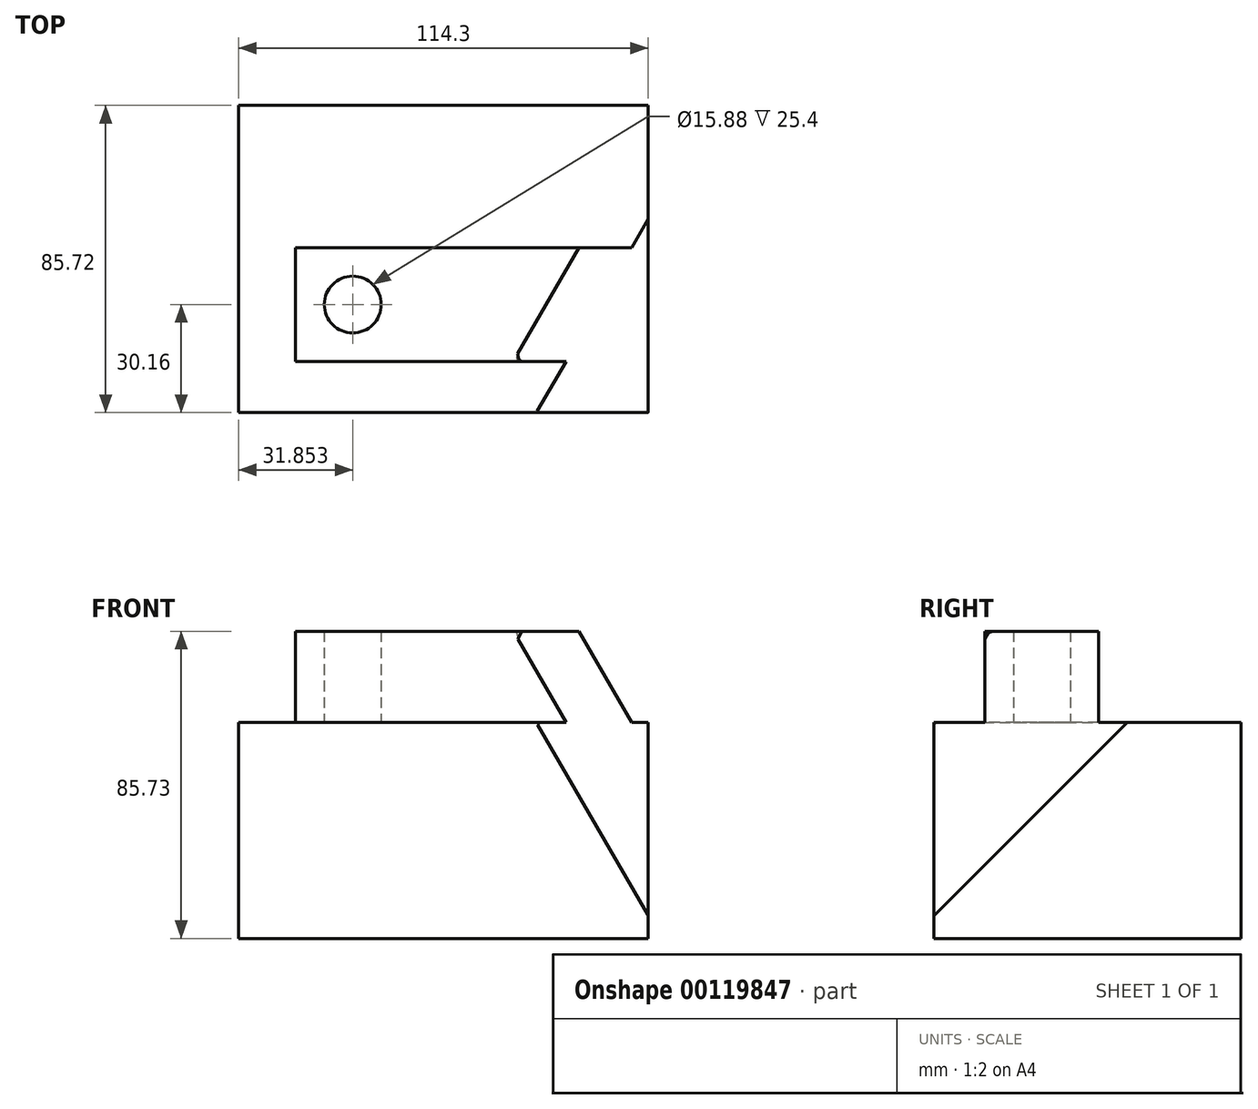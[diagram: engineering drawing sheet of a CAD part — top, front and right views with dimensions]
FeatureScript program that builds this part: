
annotation { "Feature Type Name" : "Feature", "Feature Type Description" : "" }
export const myFeature = defineFeature(function(context is Context, id is Id, definition is map)
    precondition{}
    {
        {
            var Q0;
            Q0=qCreatedBy(makeId("Front.planeOp"),FACE);
            var sketch = newSketch(context, id + "F0", { "sketchPlane" : qUnion([Q0])});
            skLineSegment(sketch, "E0", {"start": v(0, 0) * mm, "end": v(114.3, 0) * mm});
            skLineSegment(sketch, "E1", {"start": v(114.3, 0) * mm, "end": v(114.3, 60.33) * mm});
            skLineSegment(sketch, "E2", {"start": v(114.3, 60.33) * mm, "end": v(0, 60.33) * mm});
            skLineSegment(sketch, "E3", {"start": v(0, 60.33) * mm, "end": v(0, 0) * mm});
            skSolve(sketch);
        }
        {
            var Q0;
            Q0 = qSketchRegion(id + "F0", true);
            extrude(context, id + "F1", {"entities" : qUnion([Q0]), "endBound" : BoundingType.SYMMETRIC, "depth" : 85.72 * mm});
        }
        {
            var Q0;
            Q0=makeQuery(id+"F1.opExtrude","SWEPT_FACE",FACE,{"disambiguationData":[OSD([sQuery(id+"F0.wireOp",EDGE,"E2")])]});
            var sketch = newSketch(context, id + "F2", { "sketchPlane" : qUnion([Q0])});
            skLineSegment(sketch, "E4.bottom", {"start": v(15.88, 3.18) * mm, "end": v(114.3, 3.18) * mm});
            skLineSegment(sketch, "E4.top", {"start": v(15.88, -28.57) * mm, "end": v(114.3, -28.57) * mm});
            skLineSegment(sketch, "E4.left", {"start": v(15.88, 3.18) * mm, "end": v(15.88, -28.57) * mm});
            skLineSegment(sketch, "E4.right", {"start": v(114.3, 3.18) * mm, "end": v(114.3, -28.57) * mm});
            skSolve(sketch);
        }
        {
            var Q0;
            Q0 = qSketchRegion(id + "F2", true);
            extrude(context, id + "F3", {"entities" : qUnion([Q0]), "operationType" : NewBodyOperationType.ADD, "depth" : 25.4 * mm});
        }
        {
            var Q0;
            Q0=makeQuery(id+"F1.opExtrude","SWEPT_FACE",FACE,{"disambiguationData":[OSD([sQuery(id+"F0.wireOp",EDGE,"E2")])]});
            var sketch = newSketch(context, id + "F4", { "sketchPlane" : qUnion([Q0])});
            skCircle(sketch, "E5", {"center": v(31.85, -12.7) * mm, "radius": 7.94 * mm});
            skSolve(sketch);
        }
        {
            var Q0;
            Q0 = qSketchRegion(id + "F4", true);
            extrude(context, id + "F5", {"entities" : qUnion([Q0]), "operationType" : NewBodyOperationType.REMOVE, "depth" : 25.4 * mm});
        }
        {
            var Q0;
            Q0=makeQuery(id+"F3.boolean.opBoolean","MERGE",FACE,{"derivedFrom":[makeQuery(id+"F1.opExtrude","SWEPT_FACE",FACE,{"disambiguationData":[OSD([sQuery(id+"F0.wireOp",EDGE,"E1")])]}),makeQuery(id+"F3.opExtrude","SWEPT_FACE",FACE,{"disambiguationData":[OSD([sQuery(id+"F2.wireOp",EDGE,"E4.right")])]})]});
            var sketch = newSketch(context, id + "F6", { "sketchPlane" : qUnion([Q0])});
            skLineSegment(sketch, "E6", {"start": v(-42.86, 6.35) * mm, "end": v(10.9, 60.11) * mm});
            skPoint(sketch, "E7", {"position": v(-42.86, 6.35) * mm});
            skSolve(sketch);
        }
        {
            var Q0;
            Q0=makeQuery(id+"F1.opExtrude","CAP_FACE",FACE,{"disambiguationData":[OSD([sQuery(id+"F0.wireOp",EDGE,"E0"),sQuery(id+"F0.wireOp",EDGE,"E1"),sQuery(id+"F0.wireOp",EDGE,"E2"),sQuery(id+"F0.wireOp",EDGE,"E3")])],"isStart":false});
            var sketch = newSketch(context, id + "F7", { "sketchPlane" : qUnion([Q0])});
            skLineSegment(sketch, "E8", {"start": v(114.3, 6.3) * mm, "end": v(83.11, 60.33) * mm});
            skSolve(sketch);
        }
        {
            var Q0;
            Q0=sQuery(id+"F6.wireOp",VERTEX,"E7");
            var Q1;
            Q1=sQuery(id+"F7.wireOp",VERTEX,"E8.end");
            var Q2;
            Q2=sQuery(id+"F6.wireOp",VERTEX,"E6.end");
            cPlane(context, id + "F8", {"entities" : qUnion([Q0, Q1, Q2]), "cplaneType" : CPlaneType.THREE_POINT, "offset" : 25.4 * mm, "width" : 152.4 * mm, "height" : 152.4 * mm});
        }
        {
            var Q0;
            Q0=qCreatedBy(id+"F8.planeOp",FACE);
            var sketch = newSketch(context, id + "F9", { "sketchPlane" : qUnion([Q0])});
            skLineSegment(sketch, "E9", {"start": v(7.51, -51.47) * mm, "end": v(114.24, -48.75) * mm});
            skLineSegment(sketch, "E10", {"start": v(114.24, -48.75) * mm, "end": v(131.36, 53.04) * mm});
            skLineSegment(sketch, "E11", {"start": v(131.36, 53.04) * mm, "end": v(24.5, 35.06) * mm});
            skLineSegment(sketch, "E12", {"start": v(24.5, 35.06) * mm, "end": v(7.7, 10.42) * mm});
            skLineSegment(sketch, "E13", {"start": v(7.7, 10.42) * mm, "end": v(-14.9, -25.47) * mm});
            skLineSegment(sketch, "E14", {"start": v(-14.9, -25.47) * mm, "end": v(7.51, -51.47) * mm});
            skSolve(sketch);
        }
        {
            var Q0;
            Q0 = qSketchRegion(id + "F9", true);
            extrude(context, id + "F10", {"entities" : qUnion([Q0]), "operationType" : NewBodyOperationType.REMOVE, "depth" : 127 * mm});
        }
    });
